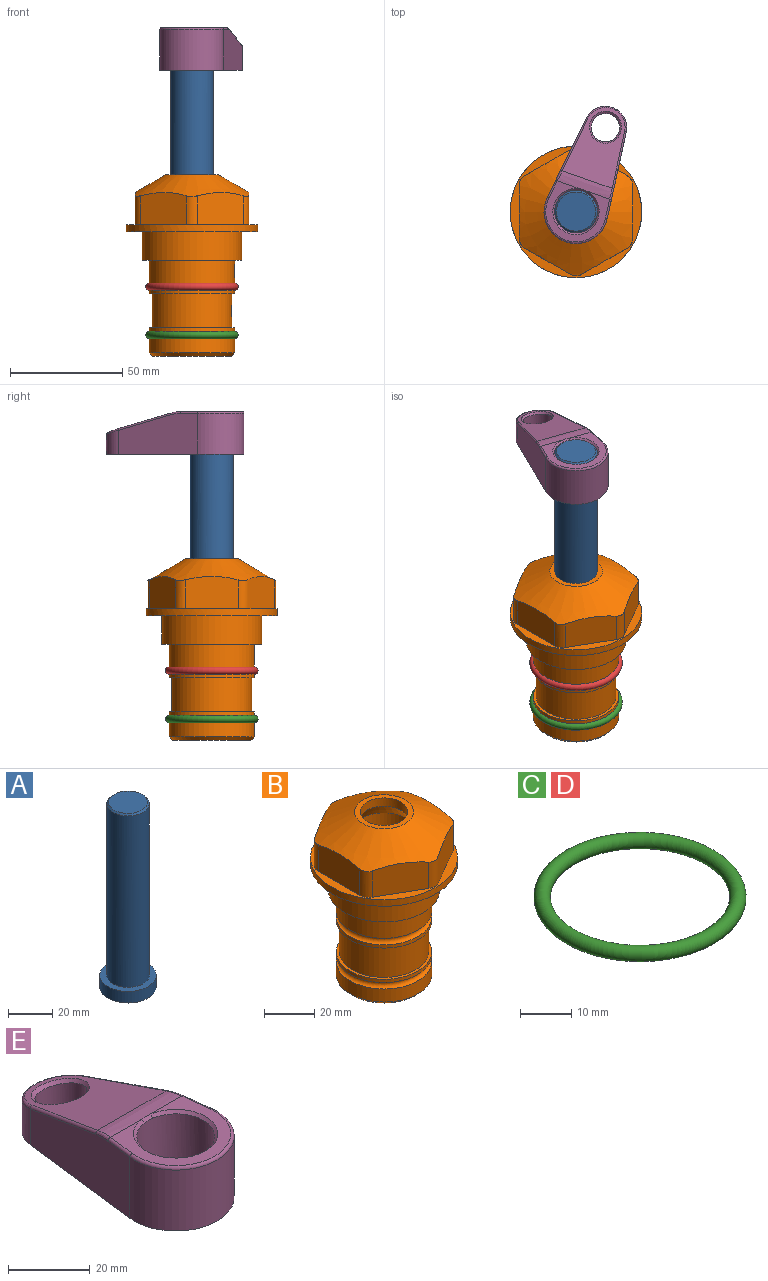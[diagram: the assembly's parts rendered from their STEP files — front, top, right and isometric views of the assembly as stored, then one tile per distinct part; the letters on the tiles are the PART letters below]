
ASSEMBLY  parts=5 mates=4
PART A: 6 faces, bbox 25.4x25.4x101.6 mm
  f0: plane 17.46x17.46mm, normal (0,0,1), area 239.5mm2, adj f5
  f1: plane 25.4x25.4mm, normal (0,0,-1), area 506.7mm2, adj f2
  f2: cylinder r=12.7mm len=25.4mm, axis (0,0,1), area 506.7mm2, adj f1,f3
  f3: plane 25.4x25.4mm, normal (0,0,1), area 221.7mm2, adj f2,f4
  f4: cylinder r=9.53mm len=94.46mm, axis (0,0,1), area 5653mm2, adj f3,f5
  f5: cone r=8.73mm half-angle=45deg, axis (0,0,-1), area 64.4mm2, adj f0,f4
PART B: 36 faces, bbox 58.7x58.7x81 mm
  f0: cylinder r=17.78mm len=35.56mm, axis (0,0,1), area 1670.8mm2, adj f23,f24,f31
  f1: cylinder r=19.05mm len=38.1mm, axis (0,0,1), area 1191.9mm2, adj f26,f27,f30
  f2: plane 58.66x58.66mm, normal (0,0,-1), area 1150.6mm2, adj f3,f28
  f3: cylinder r=29.33mm len=58.66mm, axis (0,0,-1), area 585.1mm2, adj f2,f4
  f4: plane 58.66x58.66mm, normal (0,0,1), area 475.9mm2, adj f3,f5,f6,f7,f8,f9,f10,f11
  f5: plane 20.32x14.34mm, normal (-0.5,0.87,0), area 324.4mm2, adj f4,f15,f16,f17
  f6: plane 20.32x14.34mm, normal (0.5,0.87,0), area 324.4mm2, adj f4,f14,f15,f17
  f7: plane 23.48x14.34mm, normal (1,0,0), area 324.4mm2, adj f4,f13,f14,f17
  f8: plane 20.32x14.34mm, normal (0.5,-0.87,0), area 324.4mm2, adj f4,f12,f13,f17
  f9: plane 20.32x14.34mm, normal (-0.5,-0.87,0), area 324.4mm2, adj f4,f11,f12,f17
  f10: plane 23.48x14.34mm, normal (-1,0,0), area 324.4mm2, adj f4,f11,f16,f17
  f11: cylinder r=5.08mm len=12.85mm, axis (0,0,-1), area 67.2mm2, adj f4,f9,f10,f17
  f12: cylinder r=5.08mm len=12.85mm, axis (0,0,-1), area 67.2mm2, adj f4,f8,f9,f17
  f13: cylinder r=5.08mm len=12.85mm, axis (0,0,-1), area 67.2mm2, adj f4,f7,f8,f17
  f14: cylinder r=5.08mm len=12.85mm, axis (0,0,-1), area 67.2mm2, adj f4,f6,f7,f17
  f15: cylinder r=5.08mm len=12.85mm, axis (0,0,-1), area 67.2mm2, adj f4,f5,f6,f17
  f16: cylinder r=5.08mm len=12.85mm, axis (0,0,-1), area 67.2mm2, adj f4,f5,f10,f17
  f17: cone r=11.73mm half-angle=60deg, axis (0,0,-1), area 2071.8mm2, adj f5,f6,f7,f8,f9,f10,f11,f12
  f18: plane 23.46x23.46mm, normal (0,0,1), area 147.4mm2, adj f17,f35
  f19: plane 34.93x34.93mm, normal (0,0,-1), area 958mm2, adj f29
  f20: cylinder r=19.05mm len=38.1mm, axis (0,0,1), area 760.1mm2, adj f21,f29
  f21: torus R=19.05mm, axis (0,0,1), area 565.3mm2, adj f20,f22
  f22: cylinder r=19.05mm len=38.1mm, axis (0,0,1), area 190mm2, adj f21,f23
  f23: plane 38.1x38.1mm, normal (0,0,1), area 146.9mm2, adj f0,f22
  f24: plane 38.1x38.1mm, normal (0,0,-1), area 146.9mm2, adj f0,f25
  f25: cylinder r=19.05mm len=38.1mm, axis (0,0,1), area 190mm2, adj f24,f26
  f26: torus R=19.05mm, axis (0,0,1), area 565.3mm2, adj f1,f25
  f27: plane 44.45x44.45mm, normal (0,0,-1), area 411.7mm2, adj f1,f28
  f28: cylinder r=22.23mm len=44.45mm, axis (0,0,1), area 1773.5mm2, adj f2,f27
  f29: cone r=19.05mm half-angle=45deg, axis (0,0,1), area 257.5mm2, adj f19,f20
  f30: cylinder r=3.17mm len=6.75mm, axis (-1,0,0), area 128mm2, adj f1,f33
  f31: cylinder r=3.17mm len=6.35mm, axis (-1,0,0), area 102.5mm2, adj f0,f33
  f32: plane 25.4x25.4mm, normal (0,0,1), area 506.7mm2, adj f33
  f33: cylinder r=12.7mm len=66.42mm, axis (0,0,-1), area 5236.2mm2, adj f30,f31,f32,f34
  f34: cone r=9.53mm half-angle=30deg, axis (0,0,-1), area 443.4mm2, adj f33,f35
  f35: cylinder r=9.53mm len=19.05mm, axis (0,0,-1), area 240.9mm2, adj f18,f34
PART C: 1 faces, bbox 44.7x44.7x3.2 mm
  f0: torus R=19.05mm, axis (0,0,1), area 1193.9mm2
PART D: same geometry as C
PART E: 31 faces, bbox 31.7x65.5x19.8 mm
  f0: plane 39.12x18.26mm, normal (0.99,0.12,0), area 612.2mm2, adj f1,f4,f7,f11,f13,f15
  f1: cylinder r=9.53mm len=18.91mm, axis (0,0,-1), area 296.1mm2, adj f0,f2,f7,f17
  f2: plane 39.12x18.26mm, normal (-0.99,0.12,0), area 612.2mm2, adj f1,f4,f7,f12,f14,f16
  f3: cylinder r=6.35mm len=12.7mm, axis (0,0,-1), area 362.4mm2, adj f7,f18
  f4: cylinder r=14.29mm len=28.58mm, axis (0,0,-1), area 882.2mm2, adj f0,f2,f7,f10
  f5: cylinder r=9.53mm len=19.05mm, axis (0,0,-1), area 1092.6mm2, adj f7,f19,f20
  f6: plane 26.99x23.69mm, normal (0,0,1), area 216.2mm2, adj f9,f10,f11,f12,f19
  f7: plane 63.5x28.58mm, normal (0,0,-1), area 661.8mm2, adj f0,f1,f2,f3,f4,f5,f22,f23
  f8: plane 33.52x23.6mm, normal (0,0.26,0.97), area 486mm2, adj f9,f15,f16,f17,f18
  f9: cylinder r=19.05mm len=24.72mm, axis (1,0,0), area 120.4mm2, adj f6,f8,f13,f14,f20
  f10: torus R=13.49mm, axis (0,0,1), area 59mm2, adj f4,f6,f11,f12
  f11: cylinder r=0.79mm len=8.67mm, axis (0.12,-0.99,0), area 10.8mm2, adj f0,f6,f10,f13
  f12: cylinder r=0.79mm len=8.67mm, axis (0.12,0.99,0), area 10.8mm2, adj f2,f6,f10,f14
  f13: bspline ~4.95x1.42mm, area 6.1mm2, adj f0,f9,f11,f15
  f14: bspline ~4.95x1.42mm, area 6.1mm2, adj f2,f9,f12,f16
  f15: cylinder r=0.79mm len=25.95mm, axis (0.12,-0.96,0.26), area 32.9mm2, adj f0,f8,f13,f17
  f16: cylinder r=0.79mm len=25.95mm, axis (0.12,0.96,-0.26), area 32.9mm2, adj f2,f8,f14,f17
  f17: bspline ~18.91x8.38mm, area 30mm2, adj f1,f8,f15,f16
  f18: bspline ~14.29x14.29mm, area 48.3mm2, adj f3,f8
  f19: cone r=9.53mm half-angle=45deg, axis (0,0,1), area 66.5mm2, adj f5,f6,f20
  f20: bspline ~3.22x0.96mm, area 3.5mm2, adj f5,f9,f19
  f21: plane 2.75x2.72mm, normal (0,0,-1), area 2.9mm2, adj f23,f25,f28
  f22: plane 23.05x15.88mm, normal (-0.99,-0.12,0), area 323.6mm2, adj f7,f25,f26,f27,f28,f29
  f23: plane 23.05x15.88mm, normal (0.99,-0.12,0), area 323.6mm2, adj f7,f21,f25,f27,f28,f30
  f24: cylinder r=9.53mm len=10.69mm, axis (0,0,-1), area 114.7mm2, adj f7,f27,f29,f30
  f25: cylinder r=12.7mm len=20.59mm, axis (0,0,-1), area 381.1mm2, adj f7,f21,f22,f23,f26,f28
  f26: plane 2.75x2.72mm, normal (0,0,-1), area 2.9mm2, adj f22,f25,f28
  f27: plane 19.72x18.37mm, normal (0,-0.26,-0.97), area 291.8mm2, adj f22,f23,f24,f28,f29,f30
  f28: cylinder r=15.88mm len=19.92mm, axis (1,0,0), area 54.8mm2, adj f21,f22,f23,f25,f26,f27
  f29: cylinder r=1.59mm len=11mm, axis (0,0,-1), area 34.7mm2, adj f7,f22,f24,f27
  f30: cylinder r=1.59mm len=11mm, axis (0,0,-1), area 34.7mm2, adj f7,f23,f24,f27
PLACE A rot(axis=(0,0,-1),19.3deg) t=(0,0,27.55)mm
PLACE B at identity fixed
PLACE C t=(0,0,-21.59)mm
PLACE D at identity
PLACE E rot(axis=(0,0,-1),19.3deg) t=(0,0,27.55)mm
MATE cylindrical A.f2 <-> B.f0  axis (0,0,-1) through (0,0,-10.55)mm
MATE fastened D.f0 <-> B.f0  axis (0,0,1) through (0,0,-24.51)mm
MATE fastened A.f2 <-> E.f4  axis (0,0,1) through (0,0,91.05)mm
MATE fastened C.f0 <-> B.f0  axis (0,0,1) through (0,0,-46.1)mm
